# Revit family: Fire-Hydrant
name_source: partatom
category: Specialty Equipment
units: mm (PartAtom-declared; Revit-internal decimal feet)

## family parameters
Always vertical = Yes
Classification Number = 23.65.70.17.11.11
Cut with Voids When Loaded = No
Enable Cutting in Views = No
Maintain Annotation Orientation = No
Part Type = Normal
Room Calculation Point = No
Round Connector Dimension = Use Diameter
Shared = No
Work Plane-Based = No

## types (1)
- Fire-Hydrant
    Accent Material = ARCAT - Metal - Brass
    Assembly Code = D4020300
    Bolt Material = ARCAT - Metal - Steel, Chrome Plated
    Case Material = ARCAT - Metal - Cast Iron, Painted
    Connection Type = National Standard Pumper
    Construction Details = http://www.arcat.com
    Default Elevation = 0' - 0"
    Description = Fire  Hydrant
    Expected Lifespan (Years) = 30
    Green Building-LEED = http://www.arcat.com
    Hose Connection Diameter = 0' - 2 1/2"
    Keynote = 13900
    Main Diameter = 0' - 8"
    Maintenance Schedule (Months) = 6
    Manufacturer = Generic
    Manufacturer Fax = (203) 939-2444
    Manufacturer Website = http://www.arcat.com
    Model = Generic
    Pressure (PSI) = 250
    Product Data = http://www.arcat.com
    Product Properties = http://www.arcat.com
    Pumper Nozzle Diameter = 0' - 4 1/2"
    Specification = http://www.arcat.com
    Warranty Duration (Years) = 5
    piperad = 0' - 4"

## geometry (parser evidence)
native form markers: Sweep x4
no freeform markers — native parametric forms only
